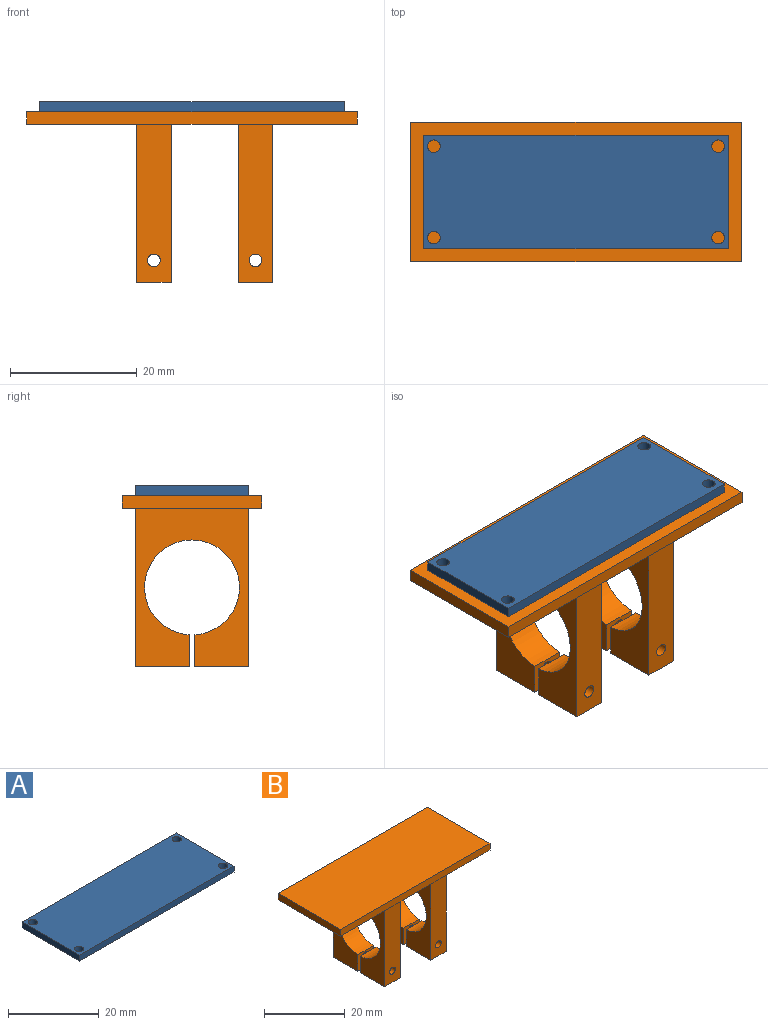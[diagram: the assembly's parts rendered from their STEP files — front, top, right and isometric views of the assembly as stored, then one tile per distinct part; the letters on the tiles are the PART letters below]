
ASSEMBLY  parts=2 mates=1
PART A: 10 faces, bbox 48.2x18x1.6 mm
  f0: plane 48.2x1.6mm, normal (0,-1,0), area 77.1mm2, adj f1,f3,f8,f9
  f1: plane 18x1.6mm, normal (1,0,0), area 28.8mm2, adj f0,f2,f8,f9
  f2: plane 48.2x1.6mm, normal (0,1,0), area 77.1mm2, adj f1,f3,f8,f9
  f3: plane 18x1.6mm, normal (-1,0,0), area 28.8mm2, adj f0,f2,f8,f9
  f4: cylinder r=1mm len=2mm, axis (0,0,-1), area 10.1mm2, adj f8,f9
  f5: cylinder r=1mm len=2mm, axis (0,0,-1), area 10.1mm2, adj f8,f9
  f6: cylinder r=1mm len=2mm, axis (0,0,-1), area 10.1mm2, adj f8,f9
  f7: cylinder r=1mm len=2mm, axis (0,0,-1), area 10.1mm2, adj f8,f9
  f8: plane 48.2x18mm, normal (0,0,1), area 855mm2, adj f0,f1,f2,f3,f4,f5,f6,f7
  f9: plane 48.2x18mm, normal (0,0,-1), area 855mm2, adj f0,f1,f2,f3,f4,f5,f6,f7
PART B: 28 faces, bbox 52.2x22x27 mm
  f0: plane 8.57x5.5mm, normal (0,0,-1), area 47.1mm2, adj f2,f9,f10,f22
  f1: plane 8.57x5.5mm, normal (0,0,-1), area 47.1mm2, adj f13,f14,f15,f20
  f2: plane 25x18mm, normal (-1,0,0), area 268.8mm2, adj f0,f3,f9,f11,f12,f21,f22,f23
  f3: plane 52.2x22mm, normal (0,0,-1), area 950.4mm2, adj f2,f4,f5,f6,f7,f9,f10,f11
  f4: plane 52.2x2mm, normal (0,1,0), area 104.4mm2, adj f3,f5,f7,f8
  f5: plane 22x2mm, normal (-1,0,0), area 44mm2, adj f3,f4,f6,f8
  f6: plane 52.2x2mm, normal (0,-1,0), area 104.4mm2, adj f3,f5,f7,f8
  f7: plane 22x2mm, normal (1,0,0), area 44mm2, adj f3,f4,f6,f8
  f8: plane 52.2x22mm, normal (0,0,1), area 1148.4mm2, adj f4,f5,f6,f7
  f9: plane 25x5.5mm, normal (0,1,0), area 134.4mm2, adj f0,f2,f3,f10,f25
  f10: plane 25x18mm, normal (1,0,0), area 268.8mm2, adj f0,f3,f9,f11,f12,f21,f22,f23
  f11: plane 25x5.5mm, normal (0,-1,0), area 134.4mm2, adj f2,f3,f10,f12,f24
  f12: plane 8.53x5.5mm, normal (0,0,-1), area 46.9mm2, adj f2,f10,f11,f23
  f13: plane 25x18mm, normal (-1,0,0), area 268.8mm2, adj f1,f3,f14,f16,f17,f18,f19,f20
  f14: plane 25x5.5mm, normal (0,1,0), area 134.4mm2, adj f1,f3,f13,f15,f26
  f15: plane 25x18mm, normal (1,0,0), area 268.8mm2, adj f1,f3,f14,f16,f17,f18,f19,f20
  f16: plane 25x5.5mm, normal (0,-1,0), area 134.4mm2, adj f3,f13,f15,f17,f27
  f17: plane 8.53x5.5mm, normal (0,0,-1), area 46.9mm2, adj f13,f15,f16,f19
  f18: cylinder r=7.5mm len=15mm, axis (-1,0,0), area 254.2mm2, adj f13,f15,f19,f20
  f19: plane 5.5x5.01mm, normal (0,1,0), area 24.4mm2, adj f13,f15,f17,f18,f27
  f20: plane 5.5x5.01mm, normal (0,-1,0), area 24.4mm2, adj f1,f13,f15,f18,f26
  f21: cylinder r=7.5mm len=15mm, axis (-1,0,0), area 254.2mm2, adj f2,f10,f22,f23
  f22: plane 5.5x5.01mm, normal (0,-1,0), area 24.4mm2, adj f0,f2,f10,f21,f25
  f23: plane 5.5x5.01mm, normal (0,1,0), area 24.4mm2, adj f2,f10,f12,f21,f24
  f24: cylinder r=1mm len=8.53mm, axis (0,1,0), area 53.6mm2, adj f11,f23
  f25: cylinder r=1mm len=8.57mm, axis (0,1,0), area 53.8mm2, adj f9,f22
  f26: cylinder r=1mm len=8.57mm, axis (0,1,0), area 53.8mm2, adj f14,f20
  f27: cylinder r=1mm len=8.53mm, axis (0,1,0), area 53.6mm2, adj f16,f19
PLACE A rot(axis=(1,0,0),180deg) t=(0,0,1.6)mm
PLACE B at identity
MATE fastened A.f8 <-> B.f8  axis (0,0,-1) through (0,0,0)mm
